# Revit family: BE_88898_de_DE
name_source: partatom
category: Leuchten
units: mm (PartAtom-declared; Revit-internal decimal feet)

## family parameters
Basisbauteil = Fläche
Beim Laden mit Abzugskörper schneiden = Ja
Bemaßung runder Anschluss = Durchmesser verwenden
Gemeinsam genutzt = Nein
Lichtquelle = Ja
Raumberechnungspunkt = Ja
Teiletyp = Normal

## types (1)
- BEGA_88898
    AC/DC = DC
    Aktualisierung = 2022-05-19T04:00:07
    Anschlussleitung = 3.0 m 05RN8-F 4 × 0,75²
    BEGA_Dummy = Nein
    BEGA_IES = Ja
    BEGA_IES1 = Ja
    BEGA_IES2 = Ja
    BEGA_IES3 = Ja
    BEGA_Intern = Ja
    BEGA_Intern_Konstruktion = Ja
    BEGA_Intern_an = Ja
    BEGA_Intern_aus = Ja
    Beschreibung = Bodeneinbauleuchte RGB
    Beschreibung_Sonderanfertigung = Hier können Sie Informationen zur Sonderanfertigung eintragen.
    Bestellnummer = 88898
    CE_Konformität = ja
    D_Breite = 0 mm  [stored 0 ft]
    D_Durchmesser = 0 mm  [stored 0 ft]
    D_Höhe = 0 mm  [stored 0 ft]
    D_Länge = 0 mm  [stored 0 ft]
    Datei für fotometrisches Netz = BE_88898.IES
    ENEC = ja
    Einbau_in_Wärmedämmung = ungeeignet
    Energieeffizienzklasse = LED A++ - A
    Farbfilter = 16777215
    Farbtemperaturverschiebung bei Dämpfen der Lampe = <Keine Auswahl>
    Gewicht = 1.7 kg
    Hersteller = BEGA
    Höhe_Platte = -97 mm
    LED_Modulbezeichnung = LED-0161/RGB
    Lampe = LED 7.2 W
    Lastklassifizierung = Beleuchtung
    Lebensdauerkriterien = L70B50 @ 25 °C =  h
    Leuchtenlichtstrom = 116 lm
    Logo = BEGA_Logo.png
    Material_06 = BEGA_Oberfläche_Edelstahl_gebürstet
    Material_11 = BEGA_Glas_opal
    Material_15 = BEGA_Leuchtmedium_matt
    Material_17 = BEGA_Reflektor
    Modell = 88898
    Neigungswinkel = 0.00°
    Oberflächentemperatur = 35 °C
    Produktdatenblatt = https://cdn.bega.com
    Schutzart = IP 67
    Schutzklasse = III
    Sonderanfertigung = Nein
    Spannung = 24 V
    Typenbild = 88898.png
    URL = https://www.bega.com
    Umgebungstemperatur = 25 °C
    Vorgabe-Ansicht = 0 mm  [stored 0 ft]

note: [stored X ft] marks values corroborated as IEEE doubles in the binary element streams (Revit-internal decimal feet)
